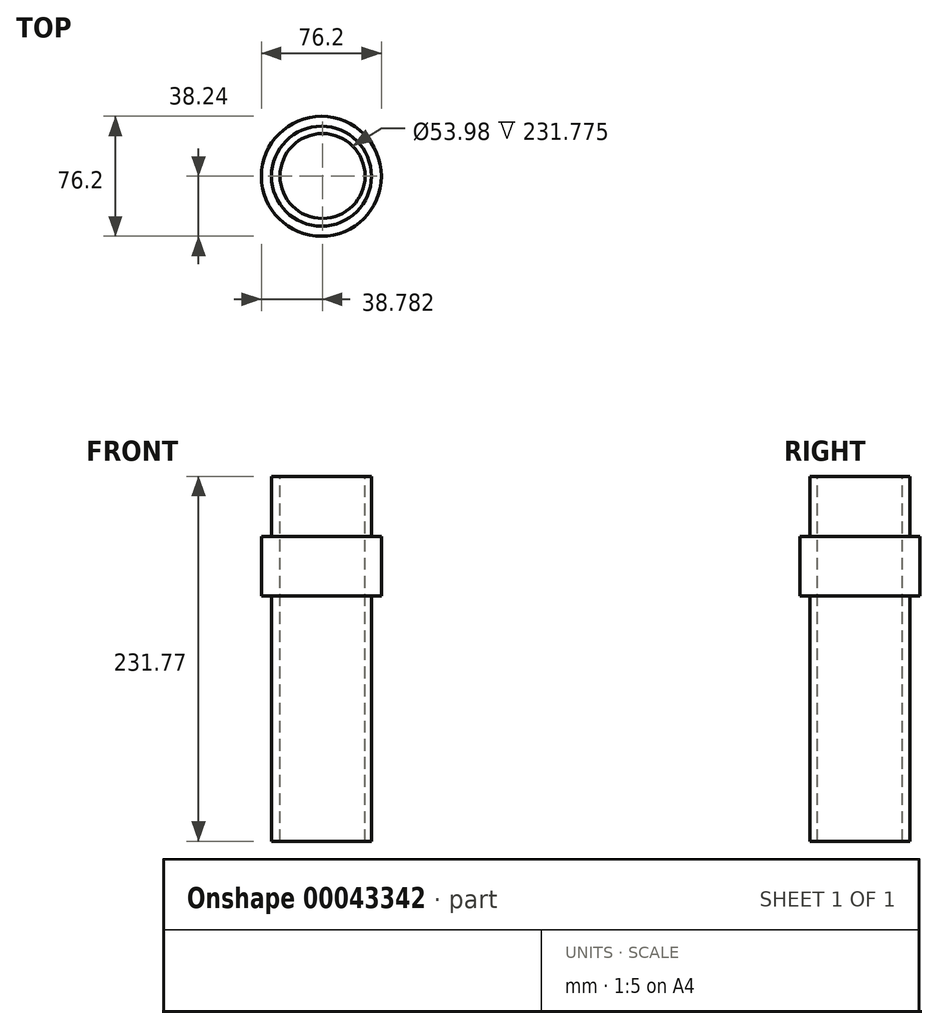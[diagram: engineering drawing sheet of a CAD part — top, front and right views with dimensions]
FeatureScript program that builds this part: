
annotation { "Feature Type Name" : "Feature", "Feature Type Description" : "" }
export const myFeature = defineFeature(function(context is Context, id is Id, definition is map)
    precondition{}
    {
        {
            var Q0;
            Q0=qCreatedBy(makeId("Front.planeOp"),FACE);
            var sketch = newSketch(context, id + "F0", { "sketchPlane" : qUnion([Q0])});
            skLineSegment(sketch, "E0.bottom", {"start": v(-31.75, 162.54) * mm, "end": v(0, 162.54) * mm});
            skLineSegment(sketch, "E0.top", {"start": v(-31.75, -69.23) * mm, "end": v(0, -69.23) * mm});
            skLineSegment(sketch, "E0.left", {"start": v(-31.75, 162.54) * mm, "end": v(-31.75, -69.23) * mm});
            skLineSegment(sketch, "E0.right", {"start": v(0, 162.54) * mm, "end": v(0, -69.23) * mm});
            skLineSegment(sketch, "E1.bottom", {"start": v(-38.1, 124.44) * mm, "end": v(-31.75, 124.44) * mm});
            skLineSegment(sketch, "E1.top", {"start": v(-38.1, 86.6) * mm, "end": v(-31.75, 86.6) * mm});
            skLineSegment(sketch, "E1.left", {"start": v(-38.1, 124.44) * mm, "end": v(-38.1, 86.6) * mm});
            skLineSegment(sketch, "E1.right", {"start": v(-31.75, 124.44) * mm, "end": v(-31.75, 86.6) * mm});
            skSolve(sketch);
        }
        {
            var Q0;
            Q0=makeQuery(id+"F0.imprint","IMPRINT",FACE,{"disambiguationData":[TD([[makeQuery(id+"F0.imprint","IMPRINT",EDGE,{"derivedFrom":sQuery(id+"F0.wireOp",EDGE,"E1.bottom")}),-1.0]])]});
            var Q1;
            {var subQ0=sQuery(id+"F0.wireOp",EDGE,"E0.bottom");Q1=makeQuery(id+"F0.imprint","IMPRINT",FACE,{"disambiguationData":[TD([[makeQuery(id+"F0.imprint","IMPRINT",EDGE,{"derivedFrom":subQ0}),-1.0]])]});}
            var Q2;
            Q2=sQuery(id+"F0.wireOp",EDGE,"E0.right");
            revolve(context, id + "F1", {"entities" : qUnion([Q0, Q1]), "axis" : qUnion([Q2]), "revolveType" : RevolveType.FULL});
        }
        {
            var Q0;
            Q0=qCreatedBy(makeId("Top.planeOp"),FACE);
            cPlane(context, id + "F2", {"entities" : qUnion([Q0]), "cplaneType" : CPlaneType.OFFSET, "offset" : 152.4 * mm, "width" : 152.4 * mm, "height" : 152.4 * mm});
        }
        {
            var Q0;
            Q0=qCreatedBy(id+"F2.planeOp",FACE);
            var sketch = newSketch(context, id + "F3", { "sketchPlane" : qUnion([Q0])});
            skCircle(sketch, "E2", {"center": v(0.68, 0.14) * mm, "radius": 26.99 * mm});
            skSolve(sketch);
        }
        {
            var Q0;
            Q0=makeQuery(id+"F3.imprint","IMPRINT",FACE,{"disambiguationData":[TD([[makeQuery(id+"F3.imprint","IMPRINT",EDGE,{"derivedFrom":sQuery(id+"F3.wireOp",EDGE,"E2")}),1.0]])]});
            var Q1;
            Q1=sQuery(id+"F3.wireOp",EDGE,"E2");
            extrude(context, id + "F4", {"entities" : qUnion([Q0]), "operationType" : NewBodyOperationType.REMOVE, "surfaceEntities" : qUnion([Q1]), "endBound" : BoundingType.SYMMETRIC, "oppositeDirection" : true, "depth" : 635 * mm});
        }
    });
